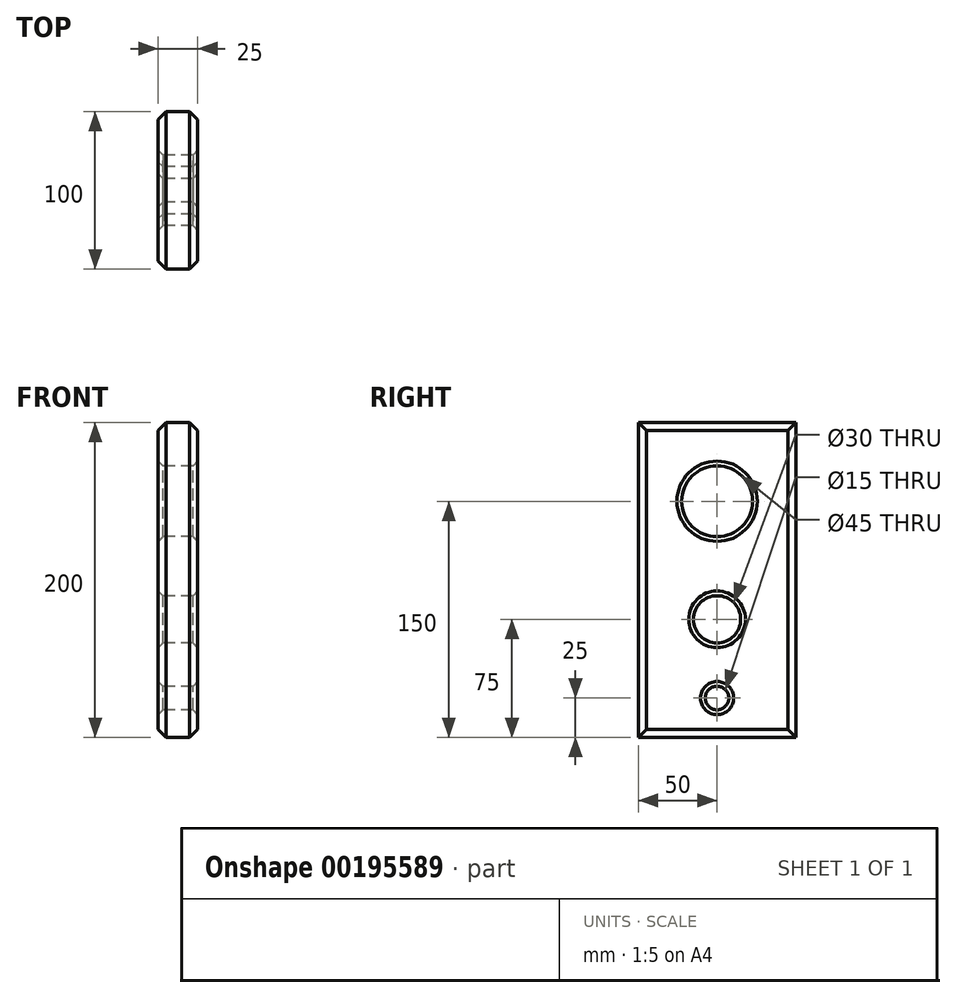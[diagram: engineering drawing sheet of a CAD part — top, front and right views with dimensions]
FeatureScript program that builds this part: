
annotation { "Feature Type Name" : "Feature", "Feature Type Description" : "" }
export const myFeature = defineFeature(function(context is Context, id is Id, definition is map)
    precondition{}
    {
        {
            var Q0;
            Q0=qCreatedBy(makeId("Right.planeOp"),FACE);
            var sketch = newSketch(context, id + "F0", { "sketchPlane" : qUnion([Q0])});
            skLineSegment(sketch, "E0.bottom", {"start": v(-50, 100) * mm, "end": v(50, 100) * mm});
            skLineSegment(sketch, "E0.top", {"start": v(-50, -100) * mm, "end": v(50, -100) * mm});
            skLineSegment(sketch, "E0.left", {"start": v(-50, 100) * mm, "end": v(-50, -100) * mm});
            skLineSegment(sketch, "E0.right", {"start": v(50, 100) * mm, "end": v(50, -100) * mm});
            skLineSegment(sketch, "E1", {"start": v(0, 100) * mm, "end": v(0, -100) * mm, "construction": true});
            skCircle(sketch, "E2", {"center": v(0, -75) * mm, "radius": 7.5 * mm});
            skCircle(sketch, "E3", {"center": v(0, 50) * mm, "radius": 22.5 * mm});
            skCircle(sketch, "E4", {"center": v(0, -25) * mm, "radius": 15 * mm});
            skSolve(sketch);
        }
        {
            var Q0;
            Q0 = qSketchRegion(id + "F0", true);
            extrude(context, id + "F1", {"entities" : qUnion([Q0]), "depth" : 25 * mm});
        }
        {
            var Q0;
            Q0=makeQuery(id+"F1.opExtrude","CAP_EDGE",EDGE,{"disambiguationData":[OSD([sQuery(id+"F0.wireOp",EDGE,"E0.right")])],"isStart":false});
            var Q1;
            Q1=makeQuery(id+"F1.opExtrude","CAP_EDGE",EDGE,{"disambiguationData":[OSD([sQuery(id+"F0.wireOp",EDGE,"E0.right")])],"isStart":true});
            var Q2;
            Q2=makeQuery(id+"F1.opExtrude","SWEPT_FACE",FACE,{"disambiguationData":[OSD([sQuery(id+"F0.wireOp",EDGE,"E3")])]});
            var Q3;
            Q3=makeQuery(id+"F1.opExtrude","SWEPT_FACE",FACE,{"disambiguationData":[OSD([sQuery(id+"F0.wireOp",EDGE,"E2")])]});
            var Q4;
            Q4=makeQuery(id+"F1.opExtrude","SWEPT_FACE",FACE,{"disambiguationData":[OSD([sQuery(id+"F0.wireOp",EDGE,"o0DREdmm-Xzoo-v8f9-7v1d-6y0Wk0DG085G")])]});
            var Q5;
            Q5=makeQuery(id+"F1.opExtrude","CAP_EDGE",EDGE,{"disambiguationData":[OSD([sQuery(id+"F0.wireOp",EDGE,"E0.left")])],"isStart":true});
            var Q6;
            Q6=makeQuery(id+"F1.opExtrude","CAP_EDGE",EDGE,{"disambiguationData":[OSD([sQuery(id+"F0.wireOp",EDGE,"E0.left")])],"isStart":false});
            var Q7;
            Q7=makeQuery(id+"F1.opExtrude","CAP_EDGE",EDGE,{"disambiguationData":[OSD([sQuery(id+"F0.wireOp",EDGE,"E0.top")])],"isStart":false});
            var Q8;
            Q8=makeQuery(id+"F1.opExtrude","CAP_EDGE",EDGE,{"disambiguationData":[OSD([sQuery(id+"F0.wireOp",EDGE,"E0.top")])],"isStart":true});
            var Q9;
            Q9=makeQuery(id+"F1.opExtrude","CAP_EDGE",EDGE,{"disambiguationData":[OSD([sQuery(id+"F0.wireOp",EDGE,"E0.bottom")])],"isStart":true});
            var Q10;
            Q10=makeQuery(id+"F1.opExtrude","CAP_EDGE",EDGE,{"disambiguationData":[OSD([sQuery(id+"F0.wireOp",EDGE,"E0.bottom")])],"isStart":false});
            chamfer(context, id + "F2", {"entities" : qUnion([Q0, Q1, Q2, Q3, Q4, Q5, Q6, Q7, Q8, Q9, Q10]), "width" : 5 * mm, "tangentPropagation" : true});
        }
        {
            var Q0;
            Q0 = qSketchRegion(id + "F0", true);
            extrude(context, id + "F3", {"entities" : qUnion([Q0]), "operationType" : NewBodyOperationType.ADD, "depth" : 25 * mm});
        }
        {
            var Q0;
            Q0=makeQuery(id+"F3.opExtrude","CAP_EDGE",EDGE,{"disambiguationData":[OSD([sQuery(id+"F0.wireOp",EDGE,"E0.bottom")])],"isStart":false});
            var Q1;
            Q1=makeQuery(id+"F3.opExtrude","CAP_EDGE",EDGE,{"disambiguationData":[OSD([sQuery(id+"F0.wireOp",EDGE,"E0.left")])],"isStart":false});
            var Q2;
            Q2=makeQuery(id+"F3.opExtrude","CAP_EDGE",EDGE,{"disambiguationData":[OSD([sQuery(id+"F0.wireOp",EDGE,"E0.top")])],"isStart":false});
            var Q3;
            Q3=makeQuery(id+"F3.opExtrude","CAP_EDGE",EDGE,{"disambiguationData":[OSD([sQuery(id+"F0.wireOp",EDGE,"E0.right")])],"isStart":false});
            var Q4;
            Q4=makeQuery(id+"F3.opExtrude","CAP_EDGE",EDGE,{"disambiguationData":[OSD([sQuery(id+"F0.wireOp",EDGE,"E0.left")])],"isStart":true});
            var Q5;
            Q5=makeQuery(id+"F3.opExtrude","CAP_EDGE",EDGE,{"disambiguationData":[OSD([sQuery(id+"F0.wireOp",EDGE,"E0.bottom")])],"isStart":true});
            var Q6;
            Q6=makeQuery(id+"F3.opExtrude","CAP_EDGE",EDGE,{"disambiguationData":[OSD([sQuery(id+"F0.wireOp",EDGE,"E0.right")])],"isStart":true});
            var Q7;
            Q7=makeQuery(id+"F3.opExtrude","CAP_EDGE",EDGE,{"disambiguationData":[OSD([sQuery(id+"F0.wireOp",EDGE,"E0.top")])],"isStart":true});
            chamfer(context, id + "F4", {"entities" : qUnion([Q0, Q1, Q2, Q3, Q4, Q5, Q6, Q7]), "width" : 5 * mm, "tangentPropagation" : true});
        }
        {
            var Q0;
            {var subQ0=sQuery(id+"F0.wireOp",EDGE,"E3");Q0=makeQuery(id+"F3.boolean.opBoolean","MERGE",FACE,{"derivedFrom":[makeQuery(id+"F1.opExtrude","SWEPT_FACE",FACE,{"disambiguationData":[OSD([subQ0])]}),makeQuery(id+"F3.opExtrude","SWEPT_FACE",FACE,{"disambiguationData":[OSD([subQ0])]})]});}
            var Q1;
            Q1=makeQuery(id+"F1.opExtrude","SWEPT_FACE",FACE,{"disambiguationData":[OSD([sQuery(id+"F0.wireOp",EDGE,"E4")])]});
            var Q2;
            {var subQ0=sQuery(id+"F0.wireOp",EDGE,"E2");Q2=makeQuery(id+"F3.boolean.opBoolean","MERGE",FACE,{"derivedFrom":[makeQuery(id+"F1.opExtrude","SWEPT_FACE",FACE,{"disambiguationData":[OSD([subQ0])]}),makeQuery(id+"F3.opExtrude","SWEPT_FACE",FACE,{"disambiguationData":[OSD([subQ0])]})]});}
            chamfer(context, id + "F5", {"entities" : qUnion([Q0, Q1, Q2]), "width" : 3 * mm, "tangentPropagation" : true});
        }
    });
